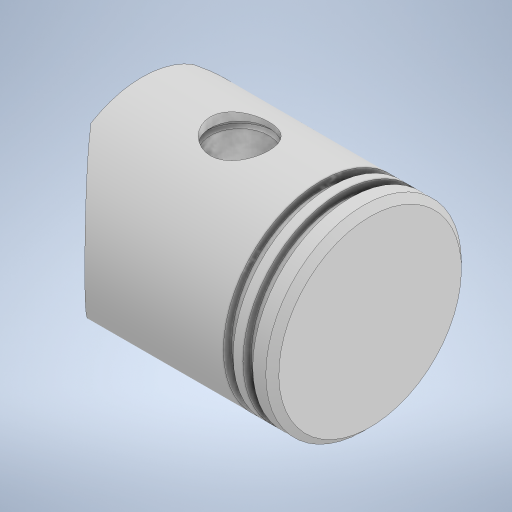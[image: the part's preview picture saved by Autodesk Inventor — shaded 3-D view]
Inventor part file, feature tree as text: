
AUTODESK INVENTOR PART (.ipt)
format: ipt  version: 2023 (Build 270158000, 158)  size: 365,568 bytes
history: native  units: mm
features: sketch x7, extrude x5, other x3, chamfer x1, fillet x1
ambient origin geometry x8: Origin, YZ Plane, XZ Plane, XY Plane, X Axis, Y Axis, Z Axis, Center Point
bodies: Body1 (feature_tree)
feature tree (17):
  other  "Sólido1"
  other  "Revolução1"
  chamfer  "Chanfro1"  Distance=6.0mm
  fillet  "Arredondamento1"  Radius=55.0mm
  extrude  "Extrusão1"  Depth=2.0mm
  extrude  "Extrusão2"  Depth=2.0mm
  extrude  "Extrusão3"  Depth=2.0mm
  extrude  "Extrusão4"  Depth=2.0mm
  extrude  "Extrusão5"  Depth=2.0mm
  other  "Revolução2"
  sketch  "Esboço1"  dims[d1=60.0mm]
  sketch  "Esboço2"  dims[d2=70.0mm]
  sketch  "Esboço3"  dims[d4=70.0mm]
  sketch  "Esboço4"  dims[d5=56.0mm]
  sketch  "Esboço5"  dims[d8=52.0mm]
  sketch  "Esboço6"  dims[d9=64.0mm]
  sketch  "Esboço8"  dims[d10=50.0mm d11=6.0mm d12=55.0mm d13=3.0mm d14=3.0mm d15=3.0mm d16=55.0mm d17=55.0mm d18=60.0mm d19=90.0deg d20=2.0mm d21=2.0mm d22=45.0deg d23=2.0mm d24=70.0mm d25=30.0mm d26=20.0mm d27=65.0mm d28=90.0mm d29=200000.0mm d30=0.0mm d32=30.0mm d33=25.0mm d34=28.0mm d35=0.0mm d36=10.0mm d37=0.0mm d38=20.0mm d39=100.0mm d40=0.0mm d41=18.0mm d42=100.0mm d43=0.0mm d45=3.0mm d46=2.0mm d47=2.0mm d49=18.0mm d50=90.0deg]
